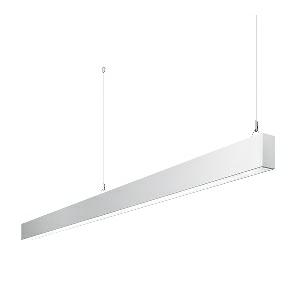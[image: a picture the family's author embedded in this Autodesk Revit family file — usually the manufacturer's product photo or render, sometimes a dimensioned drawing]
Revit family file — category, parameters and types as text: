
# Revit family: idoo_line_-_ilp_6000_830_d_end_00805746_a511
name_source: partatom
category: Lighting Fixtures
units: mm (PartAtom-declared; Revit-internal decimal feet)

## family parameters
Cut with Voids When Loaded = No
Host = Face
Light Source = No
Part Type = Normal
Room Calculation Point = No
Round Connector Dimension = Use Diameter
Shared = No

## types (1)
- IDOO.line - ILP 6000/830/D END (1 x LED, 6000 lm, 3000K)
    Apparent Load = 46 VA
    Approval mark = CE
    CIE Flux Codes = 66 91 98 40 100
    Color Rendering = 80-89
    Color Temperature = 3000K
    Control Gear = Electronic ballast
    Default Elevation = 1800 mm
    Description = ILP 6000/830/D|Suspended luminaire|light source: LED|connected load: 220-240 V, 50/60 Hz|Power consumption: approx. 46 W|standby: approx. 0,15|luminous flux: 6000 lm|luminous efficacy: 130 lm/W|light distribution: Direct/indirect|direct ratio: approx. 40 %|colour temperature: Warm white, ca. 3000 K|color rendering index (CRI): >= 80|chromaticity tolerance:  3 SDCM|System of protection: IP 40|technology: Continuously dimmable|luminaire body|material: Sectional aluminium|colour: White|lamp cover: Acrylic (PMMA), Clear|mains lead: 1,0 m With free stranded wires|Fastening: Steel cable 0.3 - 0.7 m|glare control: Prism aperture|luminance(L65): <= 2700 cd/m|unified glare rating(4H 8H): <=  16|special features: DALI Load 1x, TouchDIM - dimming via standard switch, Through-wired, up to 18 m on one mains connection, Flicker-free, Suitable as emergency lighting, Mechanical and electrical connection of the individual modules without tools|
    Frequency = 50 Hz
    Height = 110 mm
    Lamp = 1 x LED
    Lamp Light Flux = 6000 lm
    Lamp count = 1
    Length = 2250 mm
    Luminous efficacy = 130 lm/W
    Manufacturer = Waldmann
    ModVariant = No
    Model = 00805746
    Mounting Place = Ceiling
    Mounting Type = Pendant
    Number of Poles = 1
    OnlyDefault = Yes
    Power Factor = 1
    Product Name = IDOO.line - ILP 6000/830/D END
    Product group = Suspended luminaire
    ProductGroupID = 9
    Protection Class = Protection class I
    Protection Degree = IP 40
    RLX_Detail_Level = 1
    RLX_Emergency_Light_Flux = 0 lm
    RLX_Emergency_Type = 0
    RLX_Emergency_Type_DB = No
    RlxData = <blob elided: 20853 chars, md5=72b38a5e>
    Socket = socket
    Standby Power = 0 W
    System Light Flux = 6000 lm
    System Power = 46 W
    Type Comments = Product without accessories
    Type Image = 113315000-00692609.jpg
    URL = http://relux.com
    VarID = ---
    Voltage = 230 V
    Voltage Range = 220-240 V
    Weight = 0.00 kg
    Width = 60 mm  [stored 0.19685 ft]

note: [stored X ft] marks values corroborated as IEEE doubles in the binary element streams (Revit-internal decimal feet)

## geometry (parser evidence)
native form markers: Blend x4, Sweep x13
no freeform markers — native parametric forms only
